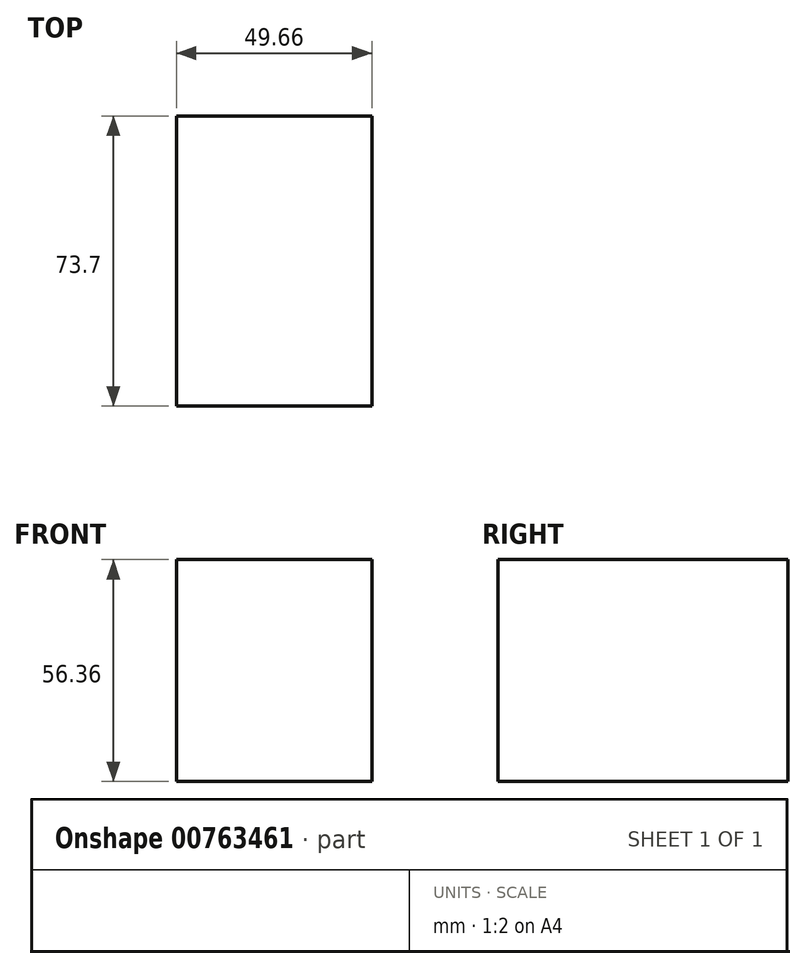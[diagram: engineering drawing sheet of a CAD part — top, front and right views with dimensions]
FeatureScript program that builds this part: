
annotation { "Feature Type Name" : "Feature", "Feature Type Description" : "" }
export const myFeature = defineFeature(function(context is Context, id is Id, definition is map)
    precondition{}
    {
        {
            var Q0;
            Q0=qCreatedBy(makeId("Top.planeOp"),FACE);
            var sketch = newSketch(context, id + "F0", { "sketchPlane" : qUnion([Q0])});
            skLineSegment(sketch, "E0.bottom", {"start": v(-22.55, 25.26) * mm, "end": v(27.11, 25.26) * mm});
            skLineSegment(sketch, "E0.top", {"start": v(-22.55, -48.44) * mm, "end": v(27.11, -48.44) * mm});
            skLineSegment(sketch, "E0.left", {"start": v(-22.55, 25.26) * mm, "end": v(-22.55, -48.44) * mm});
            skLineSegment(sketch, "E0.right", {"start": v(27.11, 25.26) * mm, "end": v(27.11, -48.44) * mm});
            skSolve(sketch);
        }
        {
            var Q0;
            Q0 = qSketchRegion(id + "F0", true);
            extrude(context, id + "F1", {"entities" : qUnion([Q0]), "depth" : 56.36 * mm, "offsetDistance" : 25.4 * mm});
        }
    });
